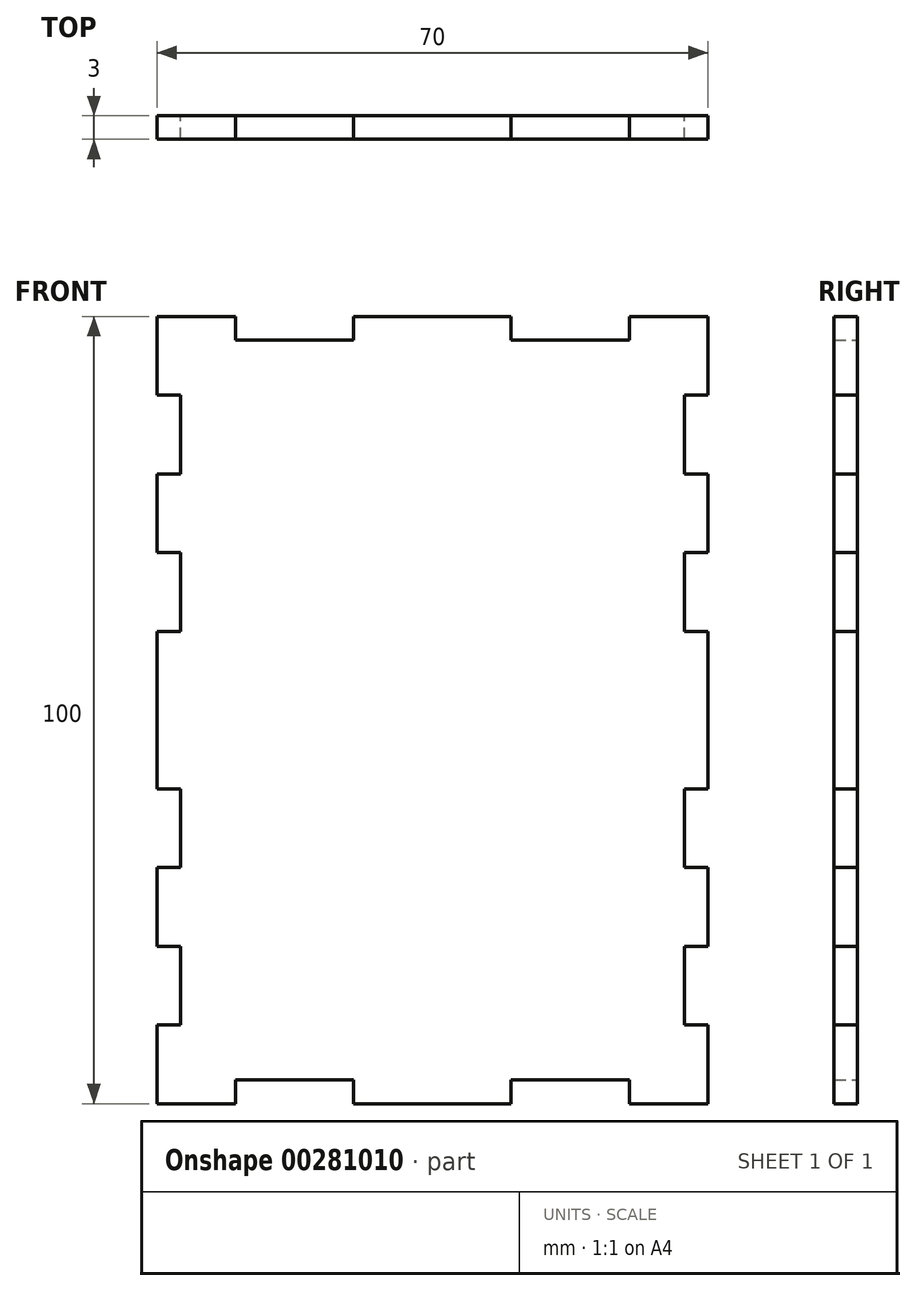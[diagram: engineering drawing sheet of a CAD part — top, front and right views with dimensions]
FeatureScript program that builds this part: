
annotation { "Feature Type Name" : "Feature", "Feature Type Description" : "" }
export const myFeature = defineFeature(function(context is Context, id is Id, definition is map)
    precondition{}
    {
        {
            var Q0;
            Q0=qCreatedBy(makeId("Front.planeOp"),FACE);
            var sketch = newSketch(context, id + "F0", { "sketchPlane" : qUnion([Q0])});
            skLineSegment(sketch, "E0.top", {"start": v(35, 50) * mm, "end": v(25, 50) * mm});
            skLineSegment(sketch, "E0.right", {"start": v(-35, -50) * mm, "end": v(-35, -40) * mm});
            skPoint(sketch, "E0.middle", {"position": v(0, 0) * mm});
            skLineSegment(sketch, "E1.bottom", {"start": v(-35, 10) * mm, "end": v(-32, 10) * mm});
            skLineSegment(sketch, "E1.top", {"start": v(-35, 20) * mm, "end": v(-32, 20) * mm});
            skLineSegment(sketch, "E1.right", {"start": v(-32, 10) * mm, "end": v(-32, 20) * mm});
            skLineSegment(sketch, "E2.bottom", {"start": v(-35, 30) * mm, "end": v(-32, 30) * mm});
            skLineSegment(sketch, "E2.top", {"start": v(-35, 40) * mm, "end": v(-32, 40) * mm});
            skLineSegment(sketch, "E2.right", {"start": v(-32, 30) * mm, "end": v(-32, 40) * mm});
            skLineSegment(sketch, "E3.trimOffspring", {"start": v(-35, 40) * mm, "end": v(-35, 50) * mm});
            skLineSegment(sketch, "E4.trimOffspring", {"start": v(-35, 20) * mm, "end": v(-35, 30) * mm});
            skLineSegment(sketch, "E5.MirrorCS", {"start": v(-35, 50) * mm, "end": v(-35, 40) * mm});
            skLineSegment(sketch, "E6.MirrorCS", {"start": v(-35, -10) * mm, "end": v(-32, -10) * mm});
            skLineSegment(sketch, "E7.MirrorCS", {"start": v(-35, -20) * mm, "end": v(-32, -20) * mm});
            skLineSegment(sketch, "E8.MirrorCS", {"start": v(-35, -40) * mm, "end": v(-32, -40) * mm});
            skLineSegment(sketch, "E9.MirrorCS", {"start": v(-35, -40) * mm, "end": v(-35, -50) * mm});
            skLineSegment(sketch, "E10.MirrorCS", {"start": v(-35, -30) * mm, "end": v(-32, -30) * mm});
            skLineSegment(sketch, "E11.MirrorCS", {"start": v(-32, -10) * mm, "end": v(-32, -20) * mm});
            skLineSegment(sketch, "E12.MirrorCS", {"start": v(-35, -20) * mm, "end": v(-35, -30) * mm});
            skLineSegment(sketch, "E13.MirrorCS", {"start": v(-32, -30) * mm, "end": v(-32, -40) * mm});
            skLineSegment(sketch, "E14.trimOffspring", {"start": v(-35, 30) * mm, "end": v(-35, 20) * mm});
            skLineSegment(sketch, "E15.trimOffspring", {"start": v(-35, 10) * mm, "end": v(-35, -10) * mm});
            skLineSegment(sketch, "E16.trimOffspring", {"start": v(-35, -10) * mm, "end": v(-35, 10) * mm});
            skLineSegment(sketch, "E17.trimOffspring", {"start": v(-35, -30) * mm, "end": v(-35, -20) * mm});
            skLineSegment(sketch, "E18.MirrorCS", {"start": v(35, -30) * mm, "end": v(32, -30) * mm});
            skLineSegment(sketch, "E19.MirrorCS", {"start": v(35, -20) * mm, "end": v(32, -20) * mm});
            skLineSegment(sketch, "E20.MirrorCS", {"start": v(35, -40) * mm, "end": v(32, -40) * mm});
            skLineSegment(sketch, "E21.MirrorCS", {"start": v(35, 10) * mm, "end": v(32, 10) * mm});
            skLineSegment(sketch, "E22.MirrorCS", {"start": v(35, 20) * mm, "end": v(32, 20) * mm});
            skLineSegment(sketch, "E23.MirrorCS", {"start": v(35, 30) * mm, "end": v(32, 30) * mm});
            skLineSegment(sketch, "E24.MirrorCS", {"start": v(35, 40) * mm, "end": v(32, 40) * mm});
            skLineSegment(sketch, "E25.MirrorCS", {"start": v(35, -10) * mm, "end": v(32, -10) * mm});
            skLineSegment(sketch, "E26.MirrorCS", {"start": v(35, 10) * mm, "end": v(35, -10) * mm});
            skLineSegment(sketch, "E27.MirrorCS", {"start": v(35, -40) * mm, "end": v(35, -50) * mm});
            skLineSegment(sketch, "E28.MirrorCS", {"start": v(35, 40) * mm, "end": v(35, 50) * mm});
            skLineSegment(sketch, "E29.MirrorCS", {"start": v(35, 20) * mm, "end": v(35, 30) * mm});
            skLineSegment(sketch, "E30.MirrorCS", {"start": v(35, -30) * mm, "end": v(35, -20) * mm});
            skLineSegment(sketch, "E31.MirrorCS", {"start": v(32, -30) * mm, "end": v(32, -40) * mm});
            skLineSegment(sketch, "E32.MirrorCS", {"start": v(32, -10) * mm, "end": v(32, -20) * mm});
            skLineSegment(sketch, "E33.MirrorCS", {"start": v(32, 30) * mm, "end": v(32, 40) * mm});
            skLineSegment(sketch, "E34.MirrorCS", {"start": v(35, 50) * mm, "end": v(35, 40) * mm});
            skLineSegment(sketch, "E35.MirrorCS", {"start": v(35, 30) * mm, "end": v(35, 20) * mm});
            skLineSegment(sketch, "E36.MirrorCS", {"start": v(32, 10) * mm, "end": v(32, 20) * mm});
            skLineSegment(sketch, "E37.MirrorCS", {"start": v(35, -50) * mm, "end": v(35, -40) * mm});
            skLineSegment(sketch, "E38.MirrorCS", {"start": v(35, -10) * mm, "end": v(35, 10) * mm});
            skLineSegment(sketch, "E39.MirrorCS", {"start": v(35, -20) * mm, "end": v(35, -30) * mm});
            skLineSegment(sketch, "E40.top", {"start": v(-10, 47) * mm, "end": v(-25, 47) * mm});
            skLineSegment(sketch, "E40.left", {"start": v(-10, 50) * mm, "end": v(-10, 47) * mm});
            skLineSegment(sketch, "E40.right", {"start": v(-25, 50) * mm, "end": v(-25, 47) * mm});
            skLineSegment(sketch, "E41.top", {"start": v(25, 47) * mm, "end": v(10, 47) * mm});
            skLineSegment(sketch, "E41.left", {"start": v(25, 50) * mm, "end": v(25, 47) * mm});
            skLineSegment(sketch, "E41.right", {"start": v(10, 50) * mm, "end": v(10, 47) * mm});
            skLineSegment(sketch, "E42.trimOffspring", {"start": v(10, 50) * mm, "end": v(-10, 50) * mm});
            skLineSegment(sketch, "E43.trimOffspring", {"start": v(-25, 50) * mm, "end": v(-35, 50) * mm});
            skPoint(sketch, "E0.bottom.start.orphan", {"position": v(35, -50) * mm});
            skLineSegment(sketch, "E44.MirrorCS", {"start": v(-25, -50) * mm, "end": v(-25, -47) * mm});
            skLineSegment(sketch, "E45.MirrorCS", {"start": v(10, -50) * mm, "end": v(10, -47) * mm});
            skLineSegment(sketch, "E46.MirrorCS", {"start": v(10, -50) * mm, "end": v(-10, -50) * mm});
            skLineSegment(sketch, "E47.MirrorCS", {"start": v(25, -50) * mm, "end": v(25, -47) * mm});
            skLineSegment(sketch, "E48.MirrorCS", {"start": v(-10, -50) * mm, "end": v(-10, -47) * mm});
            skLineSegment(sketch, "E49.MirrorCS", {"start": v(-10, -47) * mm, "end": v(-25, -47) * mm});
            skLineSegment(sketch, "E50.MirrorCS", {"start": v(-25, -50) * mm, "end": v(-35, -50) * mm});
            skLineSegment(sketch, "E51.MirrorCS", {"start": v(35, -50) * mm, "end": v(25, -50) * mm});
            skLineSegment(sketch, "E52.MirrorCS", {"start": v(25, -47) * mm, "end": v(10, -47) * mm});
            skSolve(sketch);
        }
        {
            var Q0;
            Q0 = qSketchRegion(id + "F0", true);
            extrude(context, id + "F1", {"entities" : qUnion([Q0]), "depth" : 3 * mm});
        }
    });
